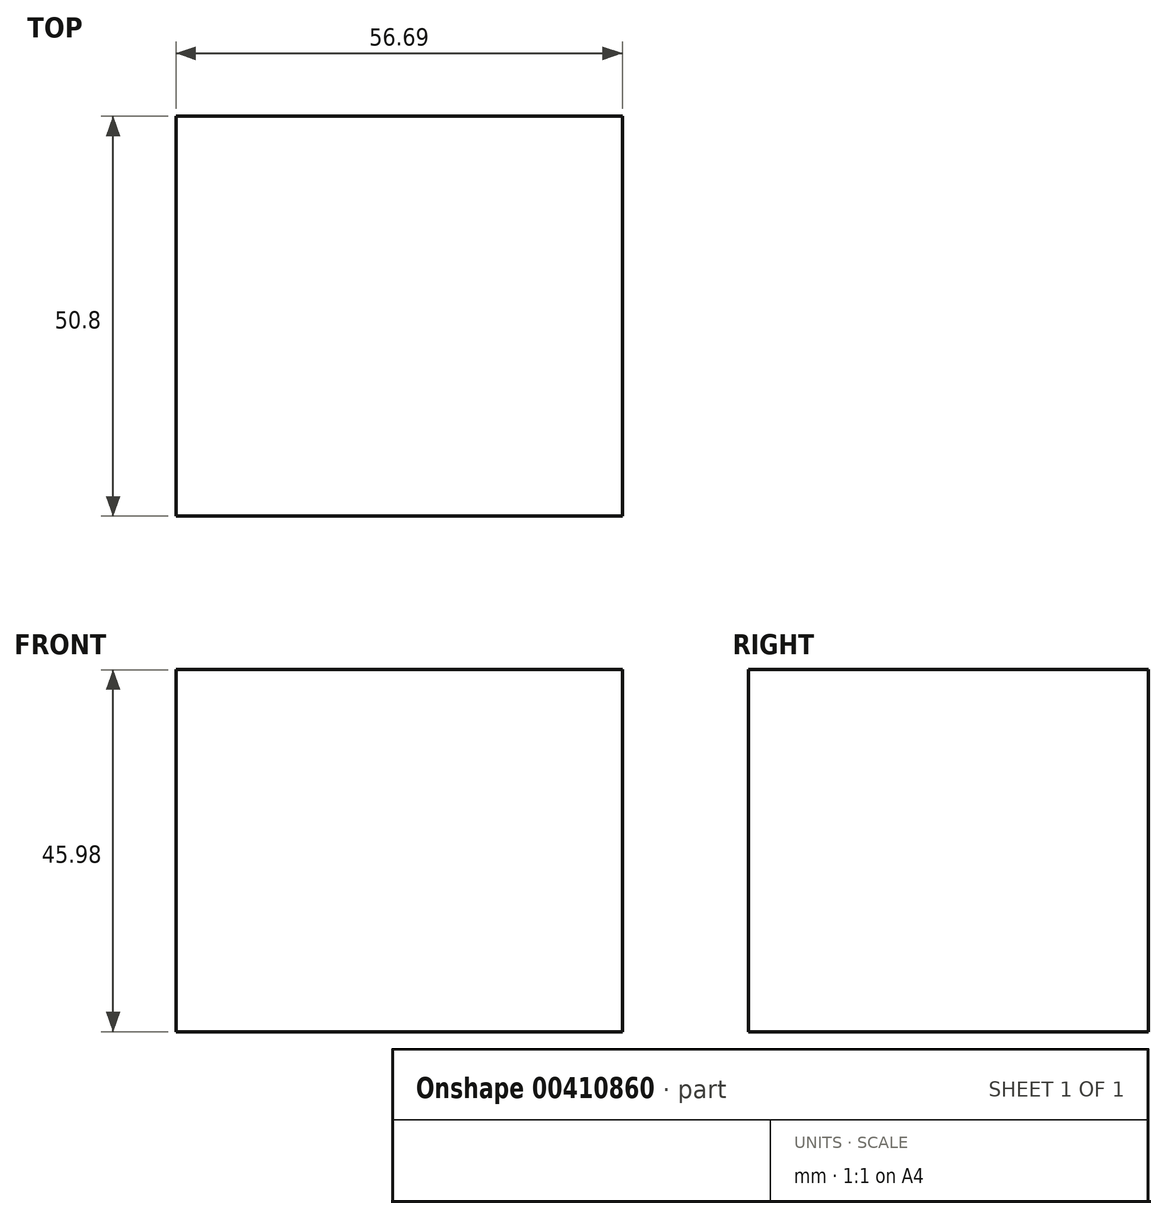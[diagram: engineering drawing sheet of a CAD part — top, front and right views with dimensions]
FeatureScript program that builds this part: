
annotation { "Feature Type Name" : "Feature", "Feature Type Description" : "" }
export const myFeature = defineFeature(function(context is Context, id is Id, definition is map)
    precondition{}
    {
        {
            var Q0;
            Q0=qCreatedBy(makeId("Front.planeOp"),FACE);
            var sketch = newSketch(context, id + "F0", { "sketchPlane" : qUnion([Q0])});
            skLineSegment(sketch, "E0.bottom", {"start": v(19.6, 18.18) * mm, "end": v(-37.08, 18.18) * mm});
            skLineSegment(sketch, "E0.top", {"start": v(19.6, 64.16) * mm, "end": v(-37.08, 64.16) * mm});
            skLineSegment(sketch, "E0.left", {"start": v(19.6, 18.18) * mm, "end": v(19.6, 64.16) * mm});
            skLineSegment(sketch, "E0.right", {"start": v(-37.08, 18.18) * mm, "end": v(-37.08, 64.16) * mm});
            skSolve(sketch);
        }
        {
            var Q0;
            Q0 = qSketchRegion(id + "F0", true);
            extrude(context, id + "F1", {"entities" : qUnion([Q0]), "depth" : 50.8 * mm});
        }
    });
